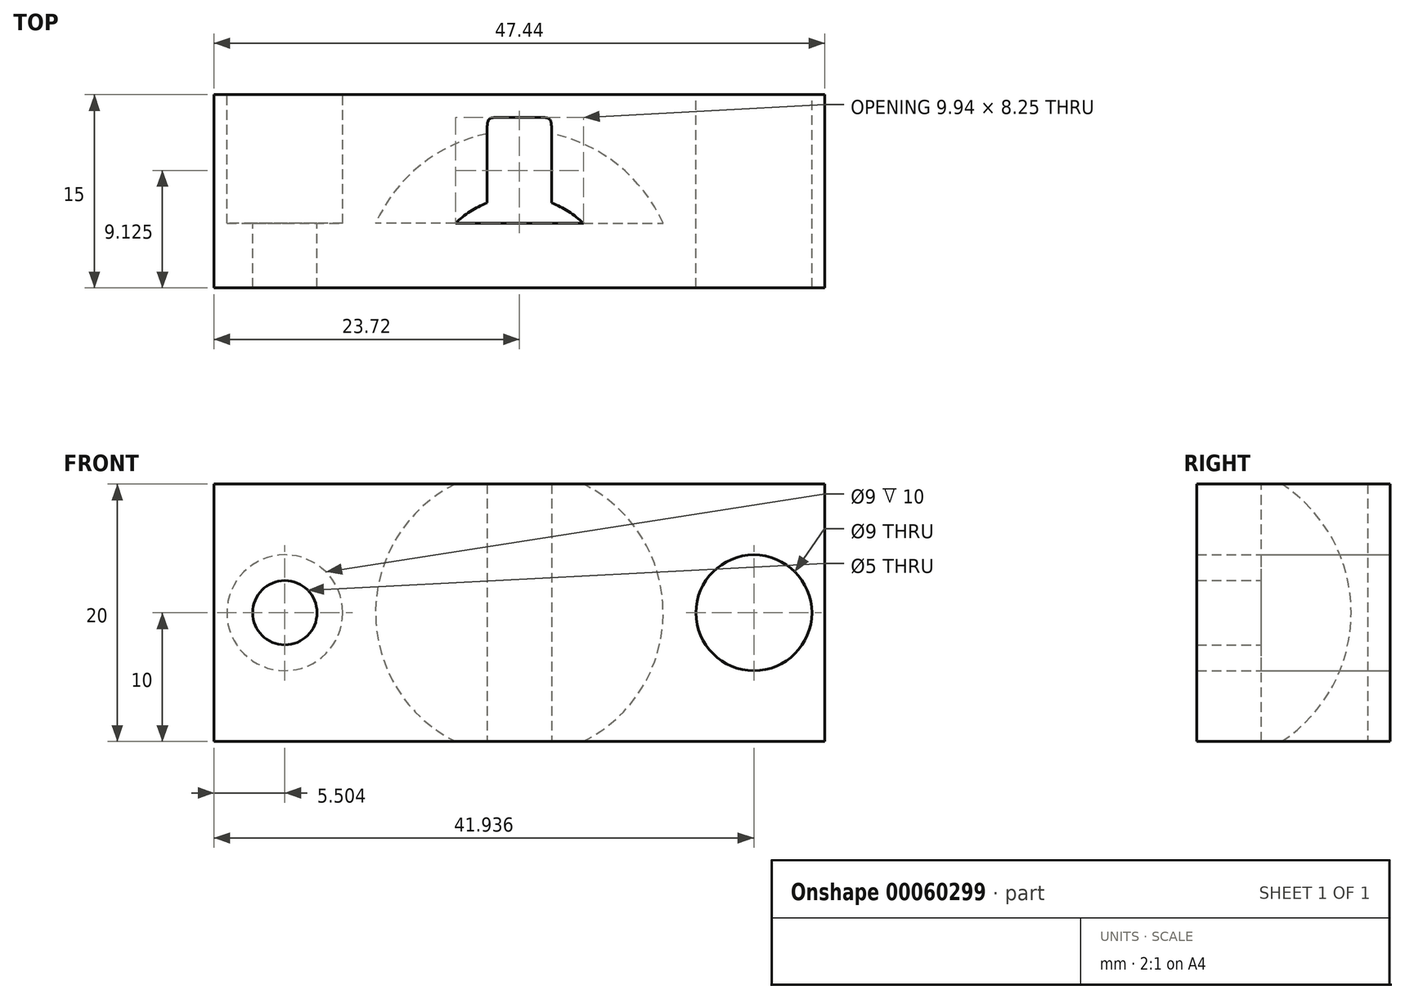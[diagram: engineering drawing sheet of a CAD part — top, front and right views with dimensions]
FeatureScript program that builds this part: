
annotation { "Feature Type Name" : "Feature", "Feature Type Description" : "" }
export const myFeature = defineFeature(function(context is Context, id is Id, definition is map)
    precondition{}
    {
        {
            var Q0;
            Q0=qCreatedBy(makeId("Front.planeOp"),FACE);
            var sketch = newSketch(context, id + "F0", { "sketchPlane" : qUnion([Q0])});
            skLineSegment(sketch, "E0.bottom", {"start": v(-23.72, 10) * mm, "end": v(23.72, 10) * mm});
            skLineSegment(sketch, "E0.top", {"start": v(-23.72, -10) * mm, "end": v(23.72, -10) * mm});
            skLineSegment(sketch, "E0.left", {"start": v(-23.72, 10) * mm, "end": v(-23.72, -10) * mm});
            skLineSegment(sketch, "E0.right", {"start": v(23.72, 10) * mm, "end": v(23.72, -10) * mm});
            skLineSegment(sketch, "E1", {"start": v(0, 10) * mm, "end": v(0, -10) * mm, "construction": true});
            skLineSegment(sketch, "E2", {"start": v(-23.72, 0) * mm, "end": v(23.72, 0) * mm, "construction": true});
            skCircle(sketch, "E3", {"center": v(-18.22, 0) * mm, "radius": 2.5 * mm});
            skCircle(sketch, "E4", {"center": v(-18.22, 0) * mm, "radius": 4.5 * mm});
            skCircle(sketch, "E5.MirrorC", {"center": v(18.22, 0) * mm, "radius": 4.5 * mm});
            skCircle(sketch, "E6.MirrorC", {"center": v(18.22, 0) * mm, "radius": 2.5 * mm});
            skSolve(sketch);
        }
        {
            var Q0;
            Q0 = qSketchRegion(id + "F0", true);
            extrude(context, id + "F1", {"entities" : qUnion([Q0]), "depth" : 15 * mm});
        }
        {
            var Q0;
            Q0=makeQuery(id+"F1.opExtrude","SWEPT_FACE",FACE,{"disambiguationData":[OSD([sQuery(id+"F0.wireOp",EDGE,"E0.bottom")])]});
            var sketch = newSketch(context, id + "F2", { "sketchPlane" : qUnion([Q0])});
            skLineSegment(sketch, "E7", {"start": v(0, 0) * mm, "end": v(0, -15) * mm, "construction": true});
            skCircle(sketch, "E8", {"center": v(0, -15) * mm, "radius": 7.05 * mm});
            skSolve(sketch);
        }
        {
            var Q0;
            Q0 = qSketchRegion(id + "F2", true);
            extrude(context, id + "F3", {"entities" : qUnion([Q0]), "operationType" : NewBodyOperationType.REMOVE, "oppositeDirection" : true, "depth" : 25 * mm});
        }
        {
            var Q0;
            {var subQ0=sQuery(id+"F0.wireOp",EDGE,"E0.bottom");var subQ1=sQuery(id+"F0.wireOp",EDGE,"E0.top");var subQ2=sQuery(id+"F0.wireOp",EDGE,"E0.left");Q0=makeQuery(id+"F3.boolean.opBoolean","SPLIT",FACE,{"disambiguationData":[TD([makeQuery(id+"F1.opExtrude","SWEPT_FACE",FACE,{"disambiguationData":[OSD([subQ2])]})])],"derivedFrom":makeQuery(id+"F1.opExtrude","CAP_FACE",FACE,{"disambiguationData":[OSD([subQ0,subQ1,subQ2,sQuery(id+"F0.wireOp",EDGE,"E0.right")])],"isStart":false})});}
            var sketch = newSketch(context, id + "F4", { "sketchPlane" : qUnion([Q0])});
            skLineSegment(sketch, "E9", {"start": v(0, 10.04) * mm, "end": v(0, -9.96) * mm});
            skArc(sketch, "E10", {"start": v(-7.05, 10) * mm, "mid": v(-12.24, 0) * mm, "end": v(-7.05, -10) * mm});
            skSolve(sketch);
        }
        {
            var Q0;
            Q0=makeQuery(id+"F4.imprint","IMPRINT",FACE,{"disambiguationData":[TD([[makeQuery(id+"F4.imprint","IMPRINT",EDGE,{"derivedFrom":sQuery(id+"F4.wireOp",EDGE,"E10")}),1.0]])]});
            var Q1;
            Q1=sQuery(id+"F4.wireOp",EDGE,"E9");
            revolve(context, id + "F5", {"operationType" : NewBodyOperationType.REMOVE, "entities" : qUnion([Q0]), "axis" : qUnion([Q1]), "revolveType" : RevolveType.FULL, "oppositeDirection" : true});
        }
        {
            var Q0;
            {var subQ0=sQuery(id+"F0.wireOp",EDGE,"E0.bottom");var subQ1=sQuery(id+"F0.wireOp",EDGE,"E0.top");var subQ2=sQuery(id+"F0.wireOp",EDGE,"E0.right");Q0=makeQuery(id+"F3.boolean.opBoolean","SPLIT",FACE,{"disambiguationData":[TD([makeQuery(id+"F1.opExtrude","SWEPT_FACE",FACE,{"disambiguationData":[OSD([subQ2])]})])],"derivedFrom":makeQuery(id+"F1.opExtrude","CAP_FACE",FACE,{"disambiguationData":[OSD([subQ0,subQ1,sQuery(id+"F0.wireOp",EDGE,"E0.left"),subQ2])],"isStart":false})});}
            var sketch = newSketch(context, id + "F6", { "sketchPlane" : qUnion([Q0])});
            skLineSegment(sketch, "E11", {"start": v(0, 10.25) * mm, "end": v(0, 10) * mm, "construction": true});
            skLineSegment(sketch, "E12.bottom", {"start": v(2.5, 10) * mm, "end": v(0, 10) * mm});
            skLineSegment(sketch, "E12.top", {"start": v(2.5, -10.08) * mm, "end": v(0, -10.08) * mm});
            skLineSegment(sketch, "E13", {"start": v(2.5, 10) * mm, "end": v(2.5, -10.08) * mm});
            skLineSegment(sketch, "E14.MirrorCS", {"start": v(-2.5, 10) * mm, "end": v(-2.5, -10.08) * mm});
            skLineSegment(sketch, "E15", {"start": v(-2.5, 10) * mm, "end": v(2.5, 10) * mm});
            skLineSegment(sketch, "E16", {"start": v(-2.5, -10.08) * mm, "end": v(2.5, -10.08) * mm});
            skSolve(sketch);
        }
        {
            var Q0;
            Q0 = qSketchRegion(id + "F6", true);
            extrude(context, id + "F7", {"entities" : qUnion([Q0]), "operationType" : NewBodyOperationType.REMOVE, "oppositeDirection" : true, "depth" : 13.25 * mm});
        }
        {
            var Q0;
            Q0=makeQuery(id+"F7.boolean.opBoolean","COPY",EDGE,{"derivedFrom":makeQuery(id+"F7.opExtrude","CAP_EDGE",EDGE,{"disambiguationData":[OSD([sQuery(id+"F6.wireOp",EDGE,"E13")])],"isStart":false})});
            var Q1;
            Q1=makeQuery(id+"F7.boolean.opBoolean","COPY",EDGE,{"derivedFrom":makeQuery(id+"F7.opExtrude","CAP_EDGE",EDGE,{"disambiguationData":[OSD([sQuery(id+"F6.wireOp",EDGE,"E14.MirrorCS")])],"isStart":false})});
            fillet(context, id + "F8", {"entities" : qUnion([Q0, Q1]), "radius" : 1 * mm, "tangentPropagation" : true, "rho" : 0.7, "crossSection" : FilletCrossSection.CONIC, "allowEdgeOverflow" : false});
        }
        {
            var Q0;
            Q0=makeQuery(id+"F0.imprint","IMPRINT",FACE,{"disambiguationData":[TD([[makeQuery(id+"F0.imprint","IMPRINT",EDGE,{"derivedFrom":sQuery(id+"F0.wireOp",EDGE,"E3")}),-1.0]])]});
            var Q1;
            Q1=makeQuery(id+"F0.imprint","IMPRINT",FACE,{"disambiguationData":[TD([[makeQuery(id+"F0.imprint","IMPRINT",EDGE,{"derivedFrom":sQuery(id+"F0.wireOp",EDGE,"E5.MirrorC")}),-1.0]])]});
            extrude(context, id + "F9", {"entities" : qUnion([Q0, Q1]), "operationType" : NewBodyOperationType.ADD, "depth" : 15 * mm, "hasSecondDirection" : true, "secondDirectionOppositeDirection" : false, "secondDirectionDepth" : 10 * mm});
        }
    });
